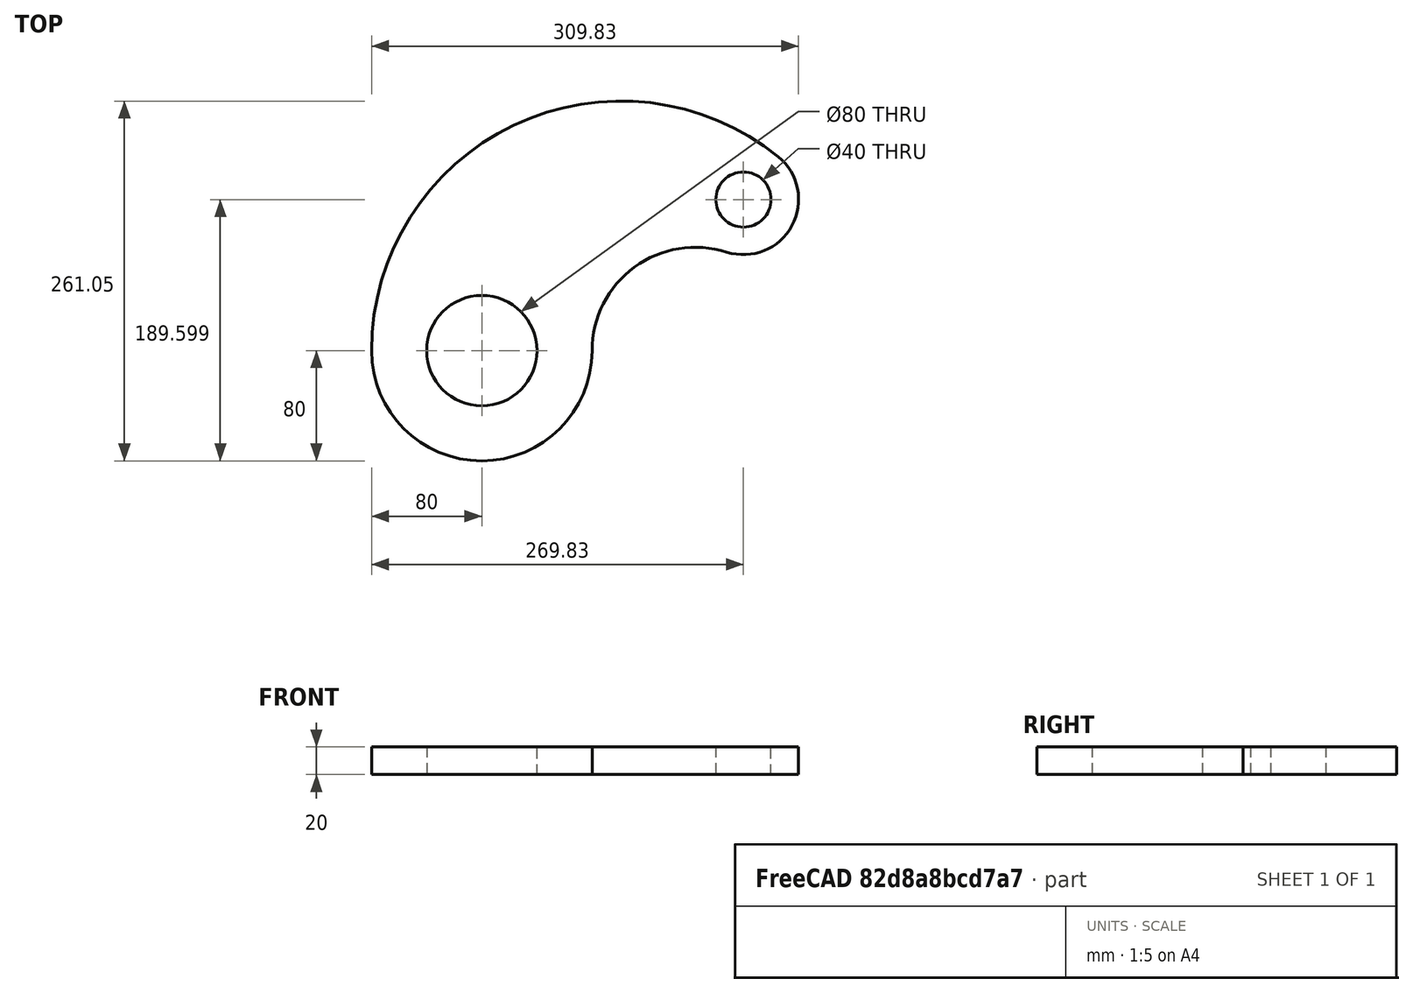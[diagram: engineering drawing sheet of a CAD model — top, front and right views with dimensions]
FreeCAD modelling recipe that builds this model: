
FCSTD DOCUMENT  (FreeCAD 0.18R4 (GitTag))
Label: Object10
License: All rights reserved
LicenseURL: http://en.wikipedia.org/wiki/All_rights_reserved
objects: Sketcher::SketchObject×1, PartDesign::Pad×1, PartDesign::Body×1
note: 4 computed .brp shape members not serialized (recipe doc carries the construction recipe); baked Part::Feature solids carry a one-line shape summary decoded from their .brp

FEATURE [Sketcher::SketchObject] Sketch
  MapMode = 5
  Support = -> [XY_Plane]
  sketch-geometry (7):
    g0: Circle CenterX=0 CenterY=0 CenterZ=0 NormalX=0 NormalY=0 NormalZ=1 AngleXU=0 Radius=40
    g1: ArcOfCircle CenterX=0 CenterY=0 CenterZ=0 NormalX=0 NormalY=0 NormalZ=1 AngleXU=0 Radius=80 StartAngle=3.14159 EndAngle=6.28319
    g2: ArcOfCircle CenterX=101.047 CenterY=0 CenterZ=0 NormalX=0 NormalY=0 NormalZ=1 AngleXU=0 Radius=181.047 StartAngle=0.889942 EndAngle=3.14159
    g3: ArcOfCircle CenterX=189.83 CenterY=109.599 CenterZ=0 NormalX=0 NormalY=0 NormalZ=1 AngleXU=0 Radius=40 StartAngle=4.40468 EndAngle=7.17313
    g4: ArcOfCircle CenterX=155 CenterY=9.2e-15 CenterZ=0 NormalX=0 NormalY=0 NormalZ=1 AngleXU=0 Radius=75 StartAngle=1.26309 EndAngle=3.14159
    g5: LineSegment [constr] StartX=0 StartY=0 StartZ=0 EndX=189.83 EndY=109.599 EndZ=0
    g6: Circle CenterX=189.83 CenterY=109.599 CenterZ=0 NormalX=0 NormalY=0 NormalZ=1 AngleXU=0 Radius=20
  constraints (17):
    c: Radius(g0) = 40
    c: Coincident(g0,g-1)
    c: Radius(g1) = 80
    c: Coincident(g1,g0)
    c: Tangent(g2,g1) = -1.5708
    c: Tangent(g3,g2) = -1.5708
    c: Radius(g4) = 75
    c: Tangent(g4,g3) = 1.5708
    c: Tangent(g4,g1) = 1.5708
    c: Coincident(g5,g0)
    c: Coincident(g5,g3)
    c: Angle(g5,g-2) = 1.0472
    c: PointOnObject(g1,g-1)
    c: PointOnObject(g1,g-1)
    c: Coincident(g6,g3)
    c: Radius(g6) = 20
    c: Radius(g3) = 40
FEATURE [PartDesign::Pad] Pad
  Length = 20
  Length2 = 100
  Profile = -> Sketch
  Type = 0
FEATURE [PartDesign::Body] Body
  Group = -> [Sketch,Pad]
  Origin = -> Origin
  Tip = -> Pad
